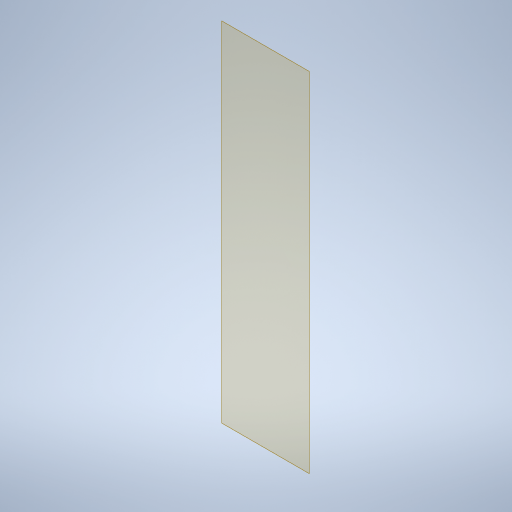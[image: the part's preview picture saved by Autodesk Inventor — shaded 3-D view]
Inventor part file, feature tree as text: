
AUTODESK INVENTOR PART (.ipt)
format: ipt  version: 2024 (Build 280153000, 153)  size: 708,096 bytes
history: native  units: mm
features: extrude x3, sketch x3, fillet x3, other x3, projected_geometry x2, plane x1, reference x1
ambient origin geometry x8: Origin, YZ Plane, XZ Plane, XY Plane, X Axis, Y Axis, Z Axis, Center Point
bodies: Solid1 (feature_tree)
feature tree (16):
  plane  "Work Plane1"
  extrude  "Extrusion1"  Depth=4.0mm
  extrude  "Extrusion2"  Depth=4.0mm
  sketch  "Sketch3"  dims[d5=0.4mm d6=8.0mm d7=45.0deg d8=11.0mm d9=4.0mm d10=0.0mm d11=9.0mm d12=0.0mm d13=8.0mm d14=5.5mm d15=5.7mm d16=2.0mm d17=0.0mm d18=0.0mm d19=9.0mm d20=2.0mm d21=1.0mm]
  fillet  "Fillet1"  Radius=0.4mm
  extrude  "Extrusion3"  Depth=8.0mm
  fillet  "Fillet2"  [1 undecoded]
  fillet  "Fillet3"  Radius=11.0mm
  sketch  "Sketch1"  dims[d0=4.0mm d1=4.0mm]
  reference  "Reference1"
  sketch  "Sketch2"  dims[d2=4.0mm d3=4.0mm d4=0.4mm]
  projected_geometry  "Projected Loop1"
  projected_geometry  "Projected Loop2"
  other  "<userpath>\Documents\Inventor\robot arm\arms\arms.iam"
  other  "arms.iam"
  other  "arm middle:1"
note: 1 required parameter value undecoded (feature->parameter linkage not recoverable at this tier; creation-order binding heuristic only, values carry confidence <= 0.55)
